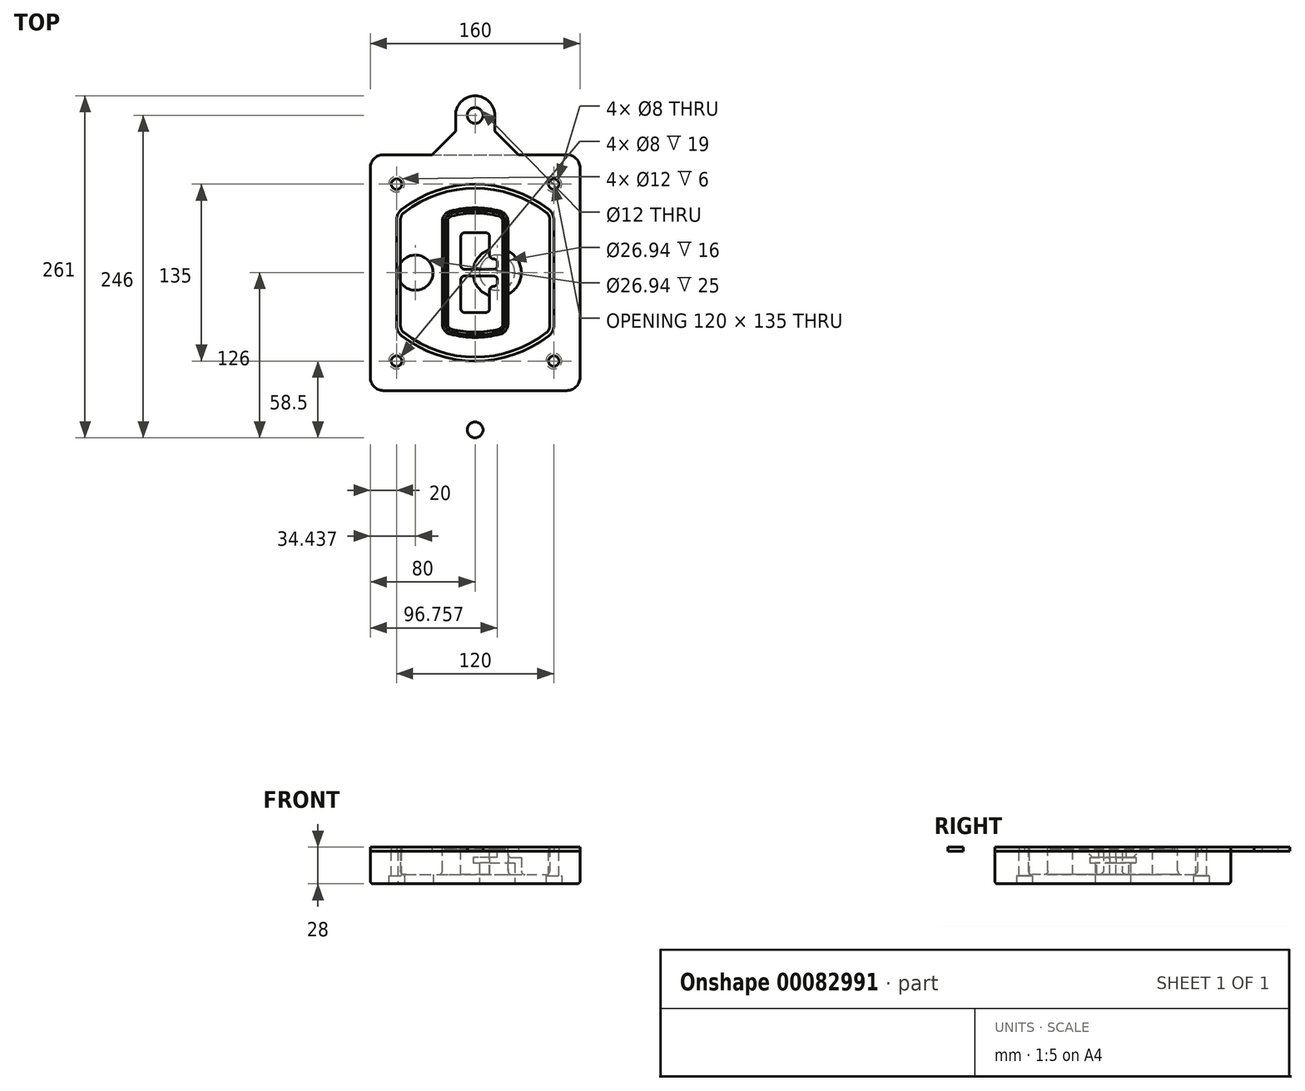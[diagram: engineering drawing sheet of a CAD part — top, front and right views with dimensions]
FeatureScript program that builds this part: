
annotation { "Feature Type Name" : "Feature", "Feature Type Description" : "" }
export const myFeature = defineFeature(function(context is Context, id is Id, definition is map)
    precondition{}
    {
        {
            var Q0;
            Q0=qCreatedBy(makeId("Top.planeOp"),FACE);
            var sketch = newSketch(context, id + "F0", { "sketchPlane" : qUnion([Q0])});
            skPoint(sketch, "E0.rect.middle", {"position": v(0, 0) * mm});
            skLineSegment(sketch, "E1.bottom", {"start": v(-70, -90) * mm, "end": v(70, -90) * mm});
            skLineSegment(sketch, "E1.top", {"start": v(-70, 90) * mm, "end": v(70, 90) * mm});
            skLineSegment(sketch, "E1.left", {"start": v(-80, -80) * mm, "end": v(-80, 80) * mm});
            skLineSegment(sketch, "E1.right", {"start": v(80, -80) * mm, "end": v(80, 80) * mm});
            skLineSegment(sketch, "E2", {"start": v(-80, 90) * mm, "end": v(80, -90) * mm, "construction": true});
            skLineSegment(sketch, "E3", {"start": v(80, 90) * mm, "end": v(-80, -90) * mm, "construction": true});
            skCircle(sketch, "E4", {"center": v(-60, 67.5) * mm, "radius": 4 * mm});
            skCircle(sketch, "E5", {"center": v(60, 67.5) * mm, "radius": 4 * mm});
            skCircle(sketch, "E6", {"center": v(60, -67.5) * mm, "radius": 4 * mm});
            skCircle(sketch, "E7", {"center": v(-60, -67.5) * mm, "radius": 4 * mm});
            skLineSegment(sketch, "E8", {"start": v(-60, 67.5) * mm, "end": v(60, 67.5) * mm, "construction": true});
            skLineSegment(sketch, "E9", {"start": v(60, 67.5) * mm, "end": v(60, -67.5) * mm, "construction": true});
            skLineSegment(sketch, "E10", {"start": v(60, -67.5) * mm, "end": v(-60, -67.5) * mm, "construction": true});
            skLineSegment(sketch, "E11", {"start": v(-60, -67.5) * mm, "end": v(-60, 67.5) * mm, "construction": true});
            skLineSegment(sketch, "E12", {"start": v(-60, 40.3) * mm, "end": v(-60, -40.3) * mm});
            skLineSegment(sketch, "E13", {"start": v(60, 40.3) * mm, "end": v(60, -40.3) * mm});
            skArc(sketch, "E14", {"start": v(56.15, 48.18) * mm, "mid": v(0, 67.5) * mm, "end": v(-56.15, 48.18) * mm});
            skArc(sketch, "E15", {"start": v(-56.15, -48.18) * mm, "mid": v(0, -67.5) * mm, "end": v(56.15, -48.18) * mm});
            skLineSegment(sketch, "E16", {"start": v(-60, 0) * mm, "end": v(60, 0) * mm, "construction": true});
            skPoint(sketch, "E17.visualSharp", {"position": v(-60, -45) * mm});
            skArc(sketch, "E17.filletArc", {"start": v(-60, -40.3) * mm, "mid": v(-58.99, -44.68) * mm, "end": v(-56.15, -48.18) * mm});
            skPoint(sketch, "E18.visualSharp", {"position": v(-60, 45) * mm});
            skArc(sketch, "E18.filletArc", {"start": v(-56.15, 48.18) * mm, "mid": v(-58.99, 44.68) * mm, "end": v(-60, 40.3) * mm});
            skPoint(sketch, "E19.visualSharp", {"position": v(60, 45) * mm});
            skArc(sketch, "E19.filletArc", {"start": v(60, 40.3) * mm, "mid": v(58.99, 44.68) * mm, "end": v(56.15, 48.18) * mm});
            skPoint(sketch, "E20.visualSharp", {"position": v(60, -45) * mm});
            skArc(sketch, "E20.filletArc", {"start": v(56.15, -48.18) * mm, "mid": v(58.99, -44.68) * mm, "end": v(60, -40.3) * mm});
            skPoint(sketch, "E21.visualSharp", {"position": v(-80, 90) * mm});
            skArc(sketch, "E21.filletArc", {"start": v(-70, 90) * mm, "mid": v(-77.07, 87.07) * mm, "end": v(-80, 80) * mm});
            skPoint(sketch, "E22.visualSharp", {"position": v(80, 90) * mm});
            skArc(sketch, "E22.filletArc", {"start": v(80, 80) * mm, "mid": v(77.07, 87.07) * mm, "end": v(70, 90) * mm});
            skPoint(sketch, "E23.visualSharp", {"position": v(80, -90) * mm});
            skArc(sketch, "E23.filletArc", {"start": v(70, -90) * mm, "mid": v(77.07, -87.07) * mm, "end": v(80, -80) * mm});
            skPoint(sketch, "E24.visualSharp", {"position": v(-80, -90) * mm});
            skArc(sketch, "E24.filletArc", {"start": v(-80, -80) * mm, "mid": v(-77.07, -87.07) * mm, "end": v(-70, -90) * mm});
            skArc(sketch, "E25.0", {"start": v(57, 40.3) * mm, "mid": v(56.3, 43.36) * mm, "end": v(54.3, 45.81) * mm});
            skLineSegment(sketch, "E25.1", {"start": v(57, 40.3) * mm, "end": v(57, -40.3) * mm});
            skArc(sketch, "E25.2", {"start": v(54.3, -45.81) * mm, "mid": v(56.3, -43.36) * mm, "end": v(57, -40.3) * mm});
            skArc(sketch, "E25.3", {"start": v(-54.3, -45.81) * mm, "mid": v(0, -64.5) * mm, "end": v(54.3, -45.81) * mm});
            skArc(sketch, "E25.4", {"start": v(-57, -40.3) * mm, "mid": v(-56.3, -43.36) * mm, "end": v(-54.3, -45.81) * mm});
            skArc(sketch, "E25.5", {"start": v(54.3, 45.81) * mm, "mid": v(0, 64.5) * mm, "end": v(-54.3, 45.81) * mm});
            skLineSegment(sketch, "E25.6", {"start": v(-57, 40.3) * mm, "end": v(-57, -40.3) * mm});
            skArc(sketch, "E25.7", {"start": v(-54.3, 45.81) * mm, "mid": v(-56.3, 43.36) * mm, "end": v(-57, 40.3) * mm});
            skArc(sketch, "E26.0", {"start": v(-58.62, 51.33) * mm, "mid": v(-62.58, 46.43) * mm, "end": v(-64, 40.3) * mm});
            skArc(sketch, "E26.1", {"start": v(58.62, 51.33) * mm, "mid": v(0, 71.5) * mm, "end": v(-58.62, 51.33) * mm});
            skArc(sketch, "E26.2", {"start": v(64, 40.3) * mm, "mid": v(62.58, 46.43) * mm, "end": v(58.62, 51.33) * mm});
            skLineSegment(sketch, "E26.3", {"start": v(64, 40.3) * mm, "end": v(64, -40.3) * mm});
            skArc(sketch, "E26.4", {"start": v(58.62, -51.33) * mm, "mid": v(62.58, -46.43) * mm, "end": v(64, -40.3) * mm});
            skLineSegment(sketch, "E26.5", {"start": v(-64, 40.3) * mm, "end": v(-64, -40.3) * mm});
            skArc(sketch, "E26.6", {"start": v(-58.62, -51.33) * mm, "mid": v(0, -71.5) * mm, "end": v(58.62, -51.33) * mm});
            skArc(sketch, "E26.7", {"start": v(-64, -40.3) * mm, "mid": v(-62.58, -46.43) * mm, "end": v(-58.62, -51.33) * mm});
            skSolve(sketch);
        }
        {
            var Q0;
            Q0=makeQuery(id+"F0.imprint","IMPRINT",FACE,{"disambiguationData":[TD([[makeQuery(id+"F0.imprint","IMPRINT",EDGE,{"derivedFrom":sQuery(id+"F0.wireOp",EDGE,"E1.bottom")}),1.0]])]});
            var Q1;
            Q1=makeQuery(id+"F0.imprint","IMPRINT",FACE,{"disambiguationData":[TD([[makeQuery(id+"F0.imprint","IMPRINT",EDGE,{"derivedFrom":sQuery(id+"F0.wireOp",EDGE,"E12")}),1.0]])]});
            var Q2;
            Q2=makeQuery(id+"F0.imprint","IMPRINT",FACE,{"disambiguationData":[TD([[makeQuery(id+"F0.imprint","IMPRINT",EDGE,{"derivedFrom":sQuery(id+"F0.wireOp",EDGE,"E25.0")}),1.0]])]});
            var Q3;
            Q3=makeQuery(id+"F0.imprint","IMPRINT",FACE,{"disambiguationData":[TD([[makeQuery(id+"F0.imprint","IMPRINT",EDGE,{"derivedFrom":sQuery(id+"F0.wireOp",EDGE,"E12")}),-1.0]])]});
            extrude(context, id + "F1", {"entities" : qUnion([Q0, Q1, Q2, Q3]), "oppositeDirection" : true, "depth" : 25 * mm});
        }
        {
            var Q0;
            Q0=makeQuery(id+"F0.imprint","IMPRINT",FACE,{"disambiguationData":[TD([[makeQuery(id+"F0.imprint","IMPRINT",EDGE,{"derivedFrom":sQuery(id+"F0.wireOp",EDGE,"E12")}),1.0]])]});
            extrude(context, id + "F2", {"entities" : qUnion([Q0]), "operationType" : NewBodyOperationType.ADD, "depth" : 3 * mm});
        }
        {
            var Q0;
            Q0=makeQuery(id+"F0.imprint","IMPRINT",FACE,{"disambiguationData":[TD([[makeQuery(id+"F0.imprint","IMPRINT",EDGE,{"derivedFrom":sQuery(id+"F0.wireOp",EDGE,"E25.0")}),1.0]])]});
            extrude(context, id + "F3", {"entities" : qUnion([Q0]), "operationType" : NewBodyOperationType.REMOVE, "oppositeDirection" : true, "depth" : 18 * mm});
        }
        {
            var Q0;
            Q0=makeQuery(id+"F2.opExtrude","CAP_FACE",FACE,{"disambiguationData":[OSD([sQuery(id+"F0.wireOp",EDGE,"E12"),sQuery(id+"F0.wireOp",EDGE,"E13"),sQuery(id+"F0.wireOp",EDGE,"E14"),sQuery(id+"F0.wireOp",EDGE,"E15"),sQuery(id+"F0.wireOp",EDGE,"E17.filletArc"),sQuery(id+"F0.wireOp",EDGE,"E18.filletArc"),sQuery(id+"F0.wireOp",EDGE,"E19.filletArc"),sQuery(id+"F0.wireOp",EDGE,"E20.filletArc"),sQuery(id+"F0.wireOp",EDGE,"E25.0"),sQuery(id+"F0.wireOp",EDGE,"E25.1"),sQuery(id+"F0.wireOp",EDGE,"E25.2"),sQuery(id+"F0.wireOp",EDGE,"E25.3"),sQuery(id+"F0.wireOp",EDGE,"E25.4"),sQuery(id+"F0.wireOp",EDGE,"E25.5"),sQuery(id+"F0.wireOp",EDGE,"E25.6"),sQuery(id+"F0.wireOp",EDGE,"E25.7")])],"isStart":false});
            var sketch = newSketch(context, id + "F4", { "sketchPlane" : qUnion([Q0])});
            skArc(sketch, "E27.0", {"start": v(-19.08, -46.97) * mm, "mid": v(0, -49.5) * mm, "end": v(19.08, -46.97) * mm});
            skArc(sketch, "E28.0", {"start": v(19.08, 46.97) * mm, "mid": v(0, 49.5) * mm, "end": v(-19.08, 46.97) * mm});
            skLineSegment(sketch, "E29", {"start": v(-25, 39.25) * mm, "end": v(-25, -39.25) * mm});
            skLineSegment(sketch, "E30", {"start": v(25, 39.25) * mm, "end": v(25, -39.25) * mm});
            skLineSegment(sketch, "E31", {"start": v(-25, 45.1) * mm, "end": v(25, 45.1) * mm, "construction": true});
            skLineSegment(sketch, "E32", {"start": v(-25, -45.1) * mm, "end": v(25, -45.1) * mm, "construction": true});
            skPoint(sketch, "E33.visualSharp", {"position": v(-25, 45.1) * mm});
            skArc(sketch, "E33.filletArc", {"start": v(-19.08, 46.97) * mm, "mid": v(-23.35, 44.11) * mm, "end": v(-25, 39.25) * mm});
            skPoint(sketch, "E34.visualSharp", {"position": v(25, 45.1) * mm});
            skArc(sketch, "E34.filletArc", {"start": v(25, 39.25) * mm, "mid": v(23.35, 44.11) * mm, "end": v(19.08, 46.97) * mm});
            skPoint(sketch, "E35.visualSharp", {"position": v(25, -45.1) * mm});
            skArc(sketch, "E35.filletArc", {"start": v(19.08, -46.97) * mm, "mid": v(23.35, -44.11) * mm, "end": v(25, -39.25) * mm});
            skPoint(sketch, "E36.visualSharp", {"position": v(-25, -45.1) * mm});
            skArc(sketch, "E36.filletArc", {"start": v(-25, -39.25) * mm, "mid": v(-23.35, -44.11) * mm, "end": v(-19.08, -46.97) * mm});
            skArc(sketch, "E37.0", {"start": v(54.3, 45.81) * mm, "mid": v(0, 64.5) * mm, "end": v(-54.3, 45.81) * mm});
            skArc(sketch, "E37.1", {"start": v(-54.3, 45.81) * mm, "mid": v(-56.3, 43.36) * mm, "end": v(-57, 40.3) * mm});
            skLineSegment(sketch, "E37.2", {"start": v(-57, 40.3) * mm, "end": v(-57, -40.3) * mm});
            skArc(sketch, "E37.3", {"start": v(-57, -40.3) * mm, "mid": v(-56.3, -43.36) * mm, "end": v(-54.3, -45.81) * mm});
            skArc(sketch, "E37.4", {"start": v(-54.3, -45.81) * mm, "mid": v(0, -64.5) * mm, "end": v(54.3, -45.81) * mm});
            skArc(sketch, "E37.5", {"start": v(54.3, -45.81) * mm, "mid": v(56.3, -43.36) * mm, "end": v(57, -40.3) * mm});
            skLineSegment(sketch, "E37.6", {"start": v(57, 40.3) * mm, "end": v(57, -40.3) * mm});
            skArc(sketch, "E37.7", {"start": v(57, 40.3) * mm, "mid": v(56.3, 43.36) * mm, "end": v(54.3, 45.81) * mm});
            skLineSegment(sketch, "E38.0", {"start": v(23, 39.25) * mm, "end": v(23, -39.25) * mm});
            skArc(sketch, "E38.1", {"start": v(18.56, -45.04) * mm, "mid": v(21.76, -42.9) * mm, "end": v(23, -39.25) * mm});
            skArc(sketch, "E38.2", {"start": v(-18.56, -45.04) * mm, "mid": v(0, -47.5) * mm, "end": v(18.56, -45.04) * mm});
            skArc(sketch, "E38.3", {"start": v(-23, -39.25) * mm, "mid": v(-21.76, -42.9) * mm, "end": v(-18.56, -45.04) * mm});
            skLineSegment(sketch, "E38.4", {"start": v(-23, 39.25) * mm, "end": v(-23, -39.25) * mm});
            skArc(sketch, "E38.5", {"start": v(23, 39.25) * mm, "mid": v(21.76, 42.9) * mm, "end": v(18.56, 45.04) * mm});
            skArc(sketch, "E38.6", {"start": v(-18.56, 45.04) * mm, "mid": v(-21.76, 42.9) * mm, "end": v(-23, 39.25) * mm});
            skArc(sketch, "E38.7", {"start": v(18.56, 45.04) * mm, "mid": v(0, 47.5) * mm, "end": v(-18.56, 45.04) * mm});
            skArc(sketch, "E39.0", {"start": v(21, 39.25) * mm, "mid": v(20.18, 41.68) * mm, "end": v(18.04, 43.1) * mm});
            skLineSegment(sketch, "E39.1", {"start": v(21, 39.25) * mm, "end": v(21, -39.25) * mm});
            skArc(sketch, "E39.2", {"start": v(18.04, -43.1) * mm, "mid": v(20.18, -41.68) * mm, "end": v(21, -39.25) * mm});
            skArc(sketch, "E39.3", {"start": v(-18.04, -43.1) * mm, "mid": v(0, -45.5) * mm, "end": v(18.04, -43.1) * mm});
            skArc(sketch, "E39.4", {"start": v(-21, -39.25) * mm, "mid": v(-20.18, -41.68) * mm, "end": v(-18.04, -43.1) * mm});
            skArc(sketch, "E39.5", {"start": v(18.04, 43.1) * mm, "mid": v(0, 45.5) * mm, "end": v(-18.04, 43.1) * mm});
            skLineSegment(sketch, "E39.6", {"start": v(-21, 39.25) * mm, "end": v(-21, -39.25) * mm});
            skArc(sketch, "E39.7", {"start": v(-18.04, 43.1) * mm, "mid": v(-20.18, 41.68) * mm, "end": v(-21, 39.25) * mm});
            skLineSegment(sketch, "E40", {"start": v(-25, 0) * mm, "end": v(25, 0) * mm, "construction": true});
            skLineSegment(sketch, "E41", {"start": v(-11, 5.5) * mm, "end": v(-11, 27.5) * mm});
            skLineSegment(sketch, "E42", {"start": v(-8, 30.5) * mm, "end": v(8, 30.5) * mm});
            skLineSegment(sketch, "E43", {"start": v(11, 27.5) * mm, "end": v(11, 13.5) * mm});
            skLineSegment(sketch, "E44", {"start": v(14, 10.5) * mm, "end": v(14, 10.5) * mm});
            skLineSegment(sketch, "E45", {"start": v(17, 7.5) * mm, "end": v(17, 5.5) * mm});
            skLineSegment(sketch, "E46", {"start": v(14, 2.5) * mm, "end": v(-8, 2.5) * mm});
            skPoint(sketch, "E47.visualSharp", {"position": v(-11, 30.5) * mm});
            skArc(sketch, "E47.filletArc", {"start": v(-8, 30.5) * mm, "mid": v(-10.12, 29.62) * mm, "end": v(-11, 27.5) * mm});
            skPoint(sketch, "E48.visualSharp", {"position": v(11, 30.5) * mm});
            skArc(sketch, "E48.filletArc", {"start": v(11, 27.5) * mm, "mid": v(10.12, 29.62) * mm, "end": v(8, 30.5) * mm});
            skPoint(sketch, "E49.visualSharp", {"position": v(11, 10.5) * mm});
            skArc(sketch, "E49.filletArc", {"start": v(11, 13.5) * mm, "mid": v(11.88, 11.38) * mm, "end": v(14, 10.5) * mm});
            skPoint(sketch, "E50.visualSharp", {"position": v(17, 10.5) * mm});
            skArc(sketch, "E50.filletArc", {"start": v(17, 7.5) * mm, "mid": v(16.12, 9.62) * mm, "end": v(14, 10.5) * mm});
            skPoint(sketch, "E51.visualSharp", {"position": v(17, 2.5) * mm});
            skArc(sketch, "E51.filletArc", {"start": v(14, 2.5) * mm, "mid": v(16.12, 3.38) * mm, "end": v(17, 5.5) * mm});
            skPoint(sketch, "E52.visualSharp", {"position": v(-11, 2.5) * mm});
            skArc(sketch, "E52.filletArc", {"start": v(-11, 5.5) * mm, "mid": v(-10.12, 3.38) * mm, "end": v(-8, 2.5) * mm});
            skLineSegment(sketch, "E53.0.MirrorCS", {"start": v(14, -2.5) * mm, "end": v(-8, -2.5) * mm});
            skArc(sketch, "E54.0.MirrorCS", {"start": v(-11, -5.5) * mm, "mid": v(-10.12, -3.38) * mm, "end": v(-8, -2.5) * mm});
            skLineSegment(sketch, "E55.0.MirrorCS", {"start": v(-11, -5.5) * mm, "end": v(-11, -27.5) * mm});
            skArc(sketch, "E56.0.MirrorCS", {"start": v(-8, -30.5) * mm, "mid": v(-10.12, -29.62) * mm, "end": v(-11, -27.5) * mm});
            skLineSegment(sketch, "E57.0.MirrorCS", {"start": v(-8, -30.5) * mm, "end": v(8, -30.5) * mm});
            skArc(sketch, "E58.0.MirrorCS", {"start": v(11, -27.5) * mm, "mid": v(10.12, -29.62) * mm, "end": v(8, -30.5) * mm});
            skLineSegment(sketch, "E59.0.MirrorCS", {"start": v(11, -27.5) * mm, "end": v(11, -13.5) * mm});
            skArc(sketch, "E60.0.MirrorCS", {"start": v(11, -13.5) * mm, "mid": v(11.88, -11.38) * mm, "end": v(14, -10.5) * mm});
            skArc(sketch, "E61.0.MirrorCS", {"start": v(17, -7.5) * mm, "mid": v(16.12, -9.62) * mm, "end": v(14, -10.5) * mm});
            skLineSegment(sketch, "E62.0.MirrorCS", {"start": v(17, -7.5) * mm, "end": v(17, -5.5) * mm});
            skArc(sketch, "E63.0.MirrorCS", {"start": v(14, -2.5) * mm, "mid": v(16.12, -3.38) * mm, "end": v(17, -5.5) * mm});
            skSolve(sketch);
        }
        {
            var Q0;
            Q0=makeQuery(id+"F4.imprint","IMPRINT",FACE,{"disambiguationData":[TD([[makeQuery(id+"F4.imprint","IMPRINT",EDGE,{"derivedFrom":sQuery(id+"F4.wireOp",EDGE,"E27.0")}),1.0]])]});
            var Q1;
            Q1=makeQuery(id+"F4.imprint","IMPRINT",FACE,{"disambiguationData":[TD([[makeQuery(id+"F4.imprint","IMPRINT",EDGE,{"derivedFrom":sQuery(id+"F4.wireOp",EDGE,"E38.0")}),-1.0]])]});
            var Q2;
            Q2=makeQuery(id+"F4.imprint","IMPRINT",FACE,{"disambiguationData":[TD([[makeQuery(id+"F4.imprint","IMPRINT",EDGE,{"derivedFrom":sQuery(id+"F4.wireOp",EDGE,"E39.0")}),1.0]])]});
            extrude(context, id + "F5", {"entities" : qUnion([Q0, Q1, Q2]), "operationType" : NewBodyOperationType.ADD, "endBound" : BoundingType.UP_TO_NEXT, "oppositeDirection" : true, "depth" : 25 * mm});
        }
        {
            var Q0;
            Q0=makeQuery(id+"F4.imprint","IMPRINT",FACE,{"disambiguationData":[TD([[makeQuery(id+"F4.imprint","IMPRINT",EDGE,{"derivedFrom":sQuery(id+"F4.wireOp",EDGE,"E38.0")}),-1.0]])]});
            extrude(context, id + "F6", {"entities" : qUnion([Q0]), "operationType" : NewBodyOperationType.REMOVE, "oppositeDirection" : true, "depth" : 2 * mm});
        }
        {
            var Q0;
            Q0=makeQuery(id+"F1.opExtrude","CAP_FACE",FACE,{"disambiguationData":[OSD([sQuery(id+"F0.wireOp",EDGE,"E1.bottom"),sQuery(id+"F0.wireOp",EDGE,"E1.top"),sQuery(id+"F0.wireOp",EDGE,"E1.left"),sQuery(id+"F0.wireOp",EDGE,"E1.right"),sQuery(id+"F0.wireOp",EDGE,"E4"),sQuery(id+"F0.wireOp",EDGE,"E5"),sQuery(id+"F0.wireOp",EDGE,"E6"),sQuery(id+"F0.wireOp",EDGE,"E7"),sQuery(id+"F0.wireOp",EDGE,"E21.filletArc"),sQuery(id+"F0.wireOp",EDGE,"E22.filletArc"),sQuery(id+"F0.wireOp",EDGE,"E23.filletArc"),sQuery(id+"F0.wireOp",EDGE,"E24.filletArc")])],"isStart":false});
            var sketch = newSketch(context, id + "F7", { "sketchPlane" : qUnion([Q0])});
            skCircle(sketch, "E64", {"center": v(16.76, 0) * mm, "radius": 13.47 * mm});
            skCircle(sketch, "E65", {"center": v(-45.56, 0) * mm, "radius": 13.47 * mm});
            skLineSegment(sketch, "E66", {"start": v(80, 0) * mm, "end": v(-80, 0) * mm});
            skCircle(sketch, "E67", {"center": v(16.76, 0) * mm, "radius": 18.47 * mm});
            skCircle(sketch, "E68", {"center": v(60, -67.5) * mm, "radius": 6 * mm});
            skCircle(sketch, "E69", {"center": v(-60, -67.5) * mm, "radius": 6 * mm});
            skCircle(sketch, "E70", {"center": v(-60, 67.5) * mm, "radius": 6 * mm});
            skCircle(sketch, "E71", {"center": v(60, 67.5) * mm, "radius": 6 * mm});
            skSolve(sketch);
        }
        {
            var Q0;
            {var subQ1=sQuery(id+"F7.wireOp",EDGE,"E66");var subQ4=sQuery(id+"F7.wireOp",EDGE,"E64");var subQ6=makeQuery(id+"F7.imprint","INTERSECT",VERTEX,{"disambiguationData":[OD(0.0)],"derivedFrom":[subQ4,subQ1]});Q0=makeQuery(id+"F7.imprint","IMPRINT",FACE,{"disambiguationData":[TD([[makeQuery(id+"F7.imprint","IMPRINT",EDGE,{"disambiguationData":[TD([[subQ6,-1.0]])],"derivedFrom":subQ4}),-1.0]])]});}
            var Q1;
            {var subQ0=sQuery(id+"F7.wireOp",EDGE,"E66");var subQ1=sQuery(id+"F7.wireOp",EDGE,"E64");var subQ3=makeQuery(id+"F7.imprint","INTERSECT",VERTEX,{"disambiguationData":[OD(0.0)],"derivedFrom":[subQ1,subQ0]});Q1=makeQuery(id+"F7.imprint","IMPRINT",FACE,{"disambiguationData":[TD([[makeQuery(id+"F7.imprint","IMPRINT",EDGE,{"disambiguationData":[TD([[subQ3,-1.0]])],"derivedFrom":subQ1}),1.0]])]});}
            var Q2;
            {var subQ0=sQuery(id+"F7.wireOp",EDGE,"E66");var subQ1=sQuery(id+"F7.wireOp",EDGE,"E64");var subQ3=makeQuery(id+"F7.imprint","INTERSECT",VERTEX,{"disambiguationData":[OD(0.0)],"derivedFrom":[subQ1,subQ0]});Q2=makeQuery(id+"F7.imprint","IMPRINT",FACE,{"disambiguationData":[TD([[makeQuery(id+"F7.imprint","IMPRINT",EDGE,{"disambiguationData":[TD([[subQ3,1.0]])],"derivedFrom":subQ1}),1.0]])]});}
            var Q3;
            {var subQ1=sQuery(id+"F7.wireOp",EDGE,"E66");var subQ4=sQuery(id+"F7.wireOp",EDGE,"E64");var subQ6=makeQuery(id+"F7.imprint","INTERSECT",VERTEX,{"disambiguationData":[OD(0.0)],"derivedFrom":[subQ4,subQ1]});Q3=makeQuery(id+"F7.imprint","IMPRINT",FACE,{"disambiguationData":[TD([[makeQuery(id+"F7.imprint","IMPRINT",EDGE,{"disambiguationData":[TD([[subQ6,1.0]])],"derivedFrom":subQ4}),-1.0]])]});}
            extrude(context, id + "F8", {"entities" : qUnion([Q0, Q1, Q2, Q3]), "operationType" : NewBodyOperationType.ADD, "oppositeDirection" : true, "depth" : 20 * mm});
        }
        {
            var Q0;
            {var subQ0=sQuery(id+"F7.wireOp",EDGE,"E66");var subQ1=sQuery(id+"F7.wireOp",EDGE,"E64");var subQ3=makeQuery(id+"F7.imprint","INTERSECT",VERTEX,{"disambiguationData":[OD(0.0)],"derivedFrom":[subQ1,subQ0]});Q0=makeQuery(id+"F7.imprint","IMPRINT",FACE,{"disambiguationData":[TD([[makeQuery(id+"F7.imprint","IMPRINT",EDGE,{"disambiguationData":[TD([[subQ3,-1.0]])],"derivedFrom":subQ1}),1.0]])]});}
            var Q1;
            {var subQ0=sQuery(id+"F7.wireOp",EDGE,"E66");var subQ1=sQuery(id+"F7.wireOp",EDGE,"E64");var subQ3=makeQuery(id+"F7.imprint","INTERSECT",VERTEX,{"disambiguationData":[OD(0.0)],"derivedFrom":[subQ1,subQ0]});Q1=makeQuery(id+"F7.imprint","IMPRINT",FACE,{"disambiguationData":[TD([[makeQuery(id+"F7.imprint","IMPRINT",EDGE,{"disambiguationData":[TD([[subQ3,1.0]])],"derivedFrom":subQ1}),1.0]])]});}
            extrude(context, id + "F9", {"entities" : qUnion([Q0, Q1]), "operationType" : NewBodyOperationType.REMOVE, "oppositeDirection" : true, "depth" : 16 * mm});
        }
        {
            var Q0;
            {var subQ0=sQuery(id+"F7.wireOp",EDGE,"E66");var subQ1=sQuery(id+"F7.wireOp",EDGE,"E65");var subQ3=makeQuery(id+"F7.imprint","INTERSECT",VERTEX,{"disambiguationData":[OD(0.0)],"derivedFrom":[subQ1,subQ0]});Q0=makeQuery(id+"F7.imprint","IMPRINT",FACE,{"disambiguationData":[TD([[makeQuery(id+"F7.imprint","IMPRINT",EDGE,{"disambiguationData":[TD([[subQ3,-1.0]])],"derivedFrom":subQ1}),1.0]])]});}
            var Q1;
            {var subQ0=sQuery(id+"F7.wireOp",EDGE,"E66");var subQ1=sQuery(id+"F7.wireOp",EDGE,"E65");var subQ3=makeQuery(id+"F7.imprint","INTERSECT",VERTEX,{"disambiguationData":[OD(0.0)],"derivedFrom":[subQ1,subQ0]});Q1=makeQuery(id+"F7.imprint","IMPRINT",FACE,{"disambiguationData":[TD([[makeQuery(id+"F7.imprint","IMPRINT",EDGE,{"disambiguationData":[TD([[subQ3,1.0]])],"derivedFrom":subQ1}),1.0]])]});}
            extrude(context, id + "F10", {"entities" : qUnion([Q0, Q1]), "operationType" : NewBodyOperationType.REMOVE, "oppositeDirection" : true, "depth" : 25 * mm});
        }
        {
            var Q0;
            Q0=makeQuery(id+"F7.imprint","IMPRINT",FACE,{"disambiguationData":[TD([[makeQuery(id+"F7.imprint","IMPRINT",EDGE,{"derivedFrom":sQuery(id+"F7.wireOp",EDGE,"E68")}),1.0]])]});
            var Q1;
            Q1=makeQuery(id+"F7.imprint","IMPRINT",FACE,{"disambiguationData":[TD([[makeQuery(id+"F7.imprint","IMPRINT",EDGE,{"derivedFrom":makeQuery(id+"F1.opExtrude","CAP_EDGE",EDGE,{"disambiguationData":[OSD([sQuery(id+"F0.wireOp",EDGE,"E5")])],"isStart":false})}),-1.0]])]});
            var Q2;
            Q2=makeQuery(id+"F7.imprint","IMPRINT",FACE,{"disambiguationData":[TD([[makeQuery(id+"F7.imprint","IMPRINT",EDGE,{"derivedFrom":sQuery(id+"F7.wireOp",EDGE,"E69")}),1.0]])]});
            var Q3;
            Q3=makeQuery(id+"F7.imprint","IMPRINT",FACE,{"disambiguationData":[TD([[makeQuery(id+"F7.imprint","IMPRINT",EDGE,{"derivedFrom":makeQuery(id+"F1.opExtrude","CAP_EDGE",EDGE,{"disambiguationData":[OSD([sQuery(id+"F0.wireOp",EDGE,"E4")])],"isStart":false})}),-1.0]])]});
            var Q4;
            Q4=makeQuery(id+"F7.imprint","IMPRINT",FACE,{"disambiguationData":[TD([[makeQuery(id+"F7.imprint","IMPRINT",EDGE,{"derivedFrom":sQuery(id+"F7.wireOp",EDGE,"E70")}),1.0]])]});
            var Q5;
            Q5=makeQuery(id+"F7.imprint","IMPRINT",FACE,{"disambiguationData":[TD([[makeQuery(id+"F7.imprint","IMPRINT",EDGE,{"derivedFrom":makeQuery(id+"F1.opExtrude","CAP_EDGE",EDGE,{"disambiguationData":[OSD([sQuery(id+"F0.wireOp",EDGE,"E7")])],"isStart":false})}),-1.0]])]});
            var Q6;
            Q6=makeQuery(id+"F7.imprint","IMPRINT",FACE,{"disambiguationData":[TD([[makeQuery(id+"F7.imprint","IMPRINT",EDGE,{"derivedFrom":sQuery(id+"F7.wireOp",EDGE,"E71")}),1.0]])]});
            var Q7;
            Q7=makeQuery(id+"F7.imprint","IMPRINT",FACE,{"disambiguationData":[TD([[makeQuery(id+"F7.imprint","IMPRINT",EDGE,{"derivedFrom":makeQuery(id+"F1.opExtrude","CAP_EDGE",EDGE,{"disambiguationData":[OSD([sQuery(id+"F0.wireOp",EDGE,"E6")])],"isStart":false})}),-1.0]])]});
            extrude(context, id + "F11", {"entities" : qUnion([Q0, Q1, Q2, Q3, Q4, Q5, Q6, Q7]), "operationType" : NewBodyOperationType.REMOVE, "oppositeDirection" : true, "depth" : 6 * mm});
        }
        {
            var Q0;
            Q0=makeQuery(id+"F9.boolean.opBoolean","COPY",FACE,{"derivedFrom":makeQuery(id+"F9.opExtrude","CAP_FACE",FACE,{"disambiguationData":[OSD([sQuery(id+"F7.wireOp",EDGE,"E64")])],"isStart":false})});
            var sketch = newSketch(context, id + "F12", { "sketchPlane" : qUnion([Q0])});
            skArc(sketch, "E72.0", {"start": v(11, 17.55) * mm, "mid": v(2.57, 11.82) * mm, "end": v(-1.54, 2.5) * mm});
            skArc(sketch, "E72.1", {"start": v(-1.54, -2.5) * mm, "mid": v(2.57, -11.82) * mm, "end": v(11, -17.55) * mm});
            skLineSegment(sketch, "E73", {"start": v(-1.54, -2.5) * mm, "end": v(14, -2.5) * mm});
            skLineSegment(sketch, "E74.0", {"start": v(14, 2.5) * mm, "end": v(-1.54, 2.5) * mm});
            skArc(sketch, "E74.1", {"start": v(14, 2.5) * mm, "mid": v(16.12, 3.38) * mm, "end": v(17, 5.5) * mm});
            skLineSegment(sketch, "E74.2", {"start": v(17, 7.5) * mm, "end": v(17, 5.5) * mm});
            skArc(sketch, "E74.3", {"start": v(17, 7.5) * mm, "mid": v(16.12, 9.62) * mm, "end": v(14, 10.5) * mm});
            skArc(sketch, "E74.4", {"start": v(11, 13.5) * mm, "mid": v(11.88, 11.38) * mm, "end": v(14, 10.5) * mm});
            skLineSegment(sketch, "E74.5", {"start": v(11, 17.55) * mm, "end": v(11, 13.5) * mm});
            skLineSegment(sketch, "E74.7", {"start": v(14, -2.5) * mm, "end": v(-1.54, -2.5) * mm});
            skArc(sketch, "E74.8", {"start": v(14, -2.5) * mm, "mid": v(16.12, -3.38) * mm, "end": v(17, -5.5) * mm});
            skLineSegment(sketch, "E74.9", {"start": v(17, -7.5) * mm, "end": v(17, -5.5) * mm});
            skArc(sketch, "E74.10", {"start": v(17, -7.5) * mm, "mid": v(16.12, -9.62) * mm, "end": v(14, -10.5) * mm});
            skArc(sketch, "E74.11", {"start": v(11, -13.5) * mm, "mid": v(11.88, -11.38) * mm, "end": v(14, -10.5) * mm});
            skLineSegment(sketch, "E74.12", {"start": v(11, -17.55) * mm, "end": v(11, -13.5) * mm});
            skPoint(sketch, "E75.orphan", {"position": v(11, -27.5) * mm});
            skPoint(sketch, "E76.orphan", {"position": v(-8, -2.5) * mm});
            skPoint(sketch, "E77.orphan", {"position": v(-8, 2.5) * mm});
            skPoint(sketch, "E78.orphan", {"position": v(11, 27.5) * mm});
            skSolve(sketch);
        }
        {
            var Q0;
            {var subQ7=sQuery(id+"F12.wireOp",EDGE,"E72.0");var subQ14=sQuery(id+"F12.wireOp",EDGE,"E72.1");var subQ16=sQuery(id+"F12.wireOp",EDGE,"E74.1");var subQ18=sQuery(id+"F12.wireOp",EDGE,"E74.8");Q0=qUnion([makeQuery(id+"F12.imprint","IMPRINT",FACE,{"disambiguationData":[TD([[makeQuery(id+"F12.imprint","IMPRINT",EDGE,{"derivedFrom":subQ7}),1.0]])]}),makeQuery(id+"F12.imprint","IMPRINT",FACE,{"disambiguationData":[TD([[makeQuery(id+"F12.imprint","IMPRINT",EDGE,{"derivedFrom":subQ14}),1.0]])]}),makeQuery(id+"F12.imprint","IMPRINT",FACE,{"disambiguationData":[TD([[makeQuery(id+"F12.imprint","IMPRINT",EDGE,{"derivedFrom":subQ16}),1.0]])]}),makeQuery(id+"F12.imprint","IMPRINT",FACE,{"disambiguationData":[TD([[makeQuery(id+"F12.imprint","IMPRINT",EDGE,{"derivedFrom":subQ18}),-1.0]])]})]);}
            var Q1;
            Q1=makeQuery(id+"F5.boolean.opBoolean","SPLIT",FACE,{"disambiguationData":[TD([makeQuery(id+"F5.opExtrude","SWEPT_FACE",FACE,{"disambiguationData":[OSD([sQuery(id+"F4.wireOp",EDGE,"E41")])]})])],"derivedFrom":makeQuery(id+"F3.boolean.opBoolean","COPY",FACE,{"derivedFrom":makeQuery(id+"F3.opExtrude","CAP_FACE",FACE,{"disambiguationData":[OSD([sQuery(id+"F0.wireOp",EDGE,"E25.0"),sQuery(id+"F0.wireOp",EDGE,"E25.1"),sQuery(id+"F0.wireOp",EDGE,"E25.2"),sQuery(id+"F0.wireOp",EDGE,"E25.3"),sQuery(id+"F0.wireOp",EDGE,"E25.4"),sQuery(id+"F0.wireOp",EDGE,"E25.5"),sQuery(id+"F0.wireOp",EDGE,"E25.6"),sQuery(id+"F0.wireOp",EDGE,"E25.7")])],"isStart":false})})});
            extrude(context, id + "F13", {"entities" : qUnion([Q0]), "operationType" : NewBodyOperationType.REMOVE, "endBound" : BoundingType.UP_TO_SURFACE, "endBoundEntityFace" : qUnion([Q1]), "depth" : 25 * mm});
        }
        {
            var Q0;
            Q0=makeQuery(id+"F3.boolean.opBoolean","COPY",EDGE,{"derivedFrom":makeQuery(id+"F3.opExtrude","CAP_EDGE",EDGE,{"disambiguationData":[OSD([sQuery(id+"F0.wireOp",EDGE,"E25.6")])],"isStart":false})});
            var Q1;
            Q1=makeQuery(id+"F8.boolean.opBoolean","INTERSECT",EDGE,{"derivedFrom":[makeQuery(id+"F5.opExtrude","SWEPT_FACE",FACE,{"disambiguationData":[OSD([sQuery(id+"F4.wireOp",EDGE,"E30")])]}),makeQuery(id+"F8.opExtrude","CAP_FACE",FACE,{"disambiguationData":[OSD([sQuery(id+"F7.wireOp",EDGE,"E67")])],"isStart":false})]});
            var Q2;
            Q2=makeQuery(id+"F8.boolean.opBoolean","INTERSECT",EDGE,{"disambiguationData":[OD(1.0)],"derivedFrom":[makeQuery(id+"F5.opExtrude","SWEPT_FACE",FACE,{"disambiguationData":[OSD([sQuery(id+"F4.wireOp",EDGE,"E30")])]}),makeQuery(id+"F8.opExtrude","SWEPT_FACE",FACE,{"disambiguationData":[OSD([sQuery(id+"F7.wireOp",EDGE,"E67")])]})]});
            var Q3;
            {var subQ0=sQuery(id+"F4.wireOp",EDGE,"E30");Q3=makeQuery(id+"F8.boolean.opBoolean","SPLIT",EDGE,{"disambiguationData":[TD([makeQuery(id+"F5.opExtrude","SWEPT_FACE",FACE,{"disambiguationData":[OSD([sQuery(id+"F4.wireOp",EDGE,"E35.filletArc")])]})])],"derivedFrom":makeQuery(id+"F5.opExtrude","CAP_EDGE",EDGE,{"disambiguationData":[OSD([subQ0])],"isStart":false})});}
            var Q4;
            {var subQ0=sQuery(id+"F0.wireOp",EDGE,"E25.7");var subQ1=sQuery(id+"F0.wireOp",EDGE,"E25.1");var subQ2=sQuery(id+"F0.wireOp",EDGE,"E25.6");var subQ3=sQuery(id+"F0.wireOp",EDGE,"E25.5");var subQ4=sQuery(id+"F0.wireOp",EDGE,"E25.4");var subQ5=sQuery(id+"F0.wireOp",EDGE,"E25.0");var subQ6=sQuery(id+"F0.wireOp",EDGE,"E25.2");var subQ7=sQuery(id+"F0.wireOp",EDGE,"E25.3");Q4=makeQuery(id+"F8.boolean.opBoolean","INTERSECT",EDGE,{"derivedFrom":[makeQuery(id+"F5.boolean.opBoolean","SPLIT",FACE,{"disambiguationData":[TD([makeQuery(id+"F2.opExtrude","SWEPT_FACE",FACE,{"disambiguationData":[OSD([subQ5])]})])],"derivedFrom":makeQuery(id+"F3.boolean.opBoolean","COPY",FACE,{"derivedFrom":makeQuery(id+"F3.opExtrude","CAP_FACE",FACE,{"disambiguationData":[OSD([subQ5,subQ1,subQ6,subQ7,subQ4,subQ3,subQ2,subQ0])],"isStart":false})})}),makeQuery(id+"F8.opExtrude","SWEPT_FACE",FACE,{"disambiguationData":[OSD([sQuery(id+"F7.wireOp",EDGE,"E67")])]})]});}
            var Q5;
            Q5=makeQuery(id+"F8.boolean.opBoolean","INTERSECT",EDGE,{"disambiguationData":[OD(0.0)],"derivedFrom":[makeQuery(id+"F5.opExtrude","SWEPT_FACE",FACE,{"disambiguationData":[OSD([sQuery(id+"F4.wireOp",EDGE,"E30")])]}),makeQuery(id+"F8.opExtrude","SWEPT_FACE",FACE,{"disambiguationData":[OSD([sQuery(id+"F7.wireOp",EDGE,"E67")])]})]});
            fillet(context, id + "F14", {"entities" : qUnion([Q0, Q1, Q2, Q3, Q4, Q5]), "radius" : 3 * mm, "tangentPropagation" : true, "allowEdgeOverflow" : false});
        }
        {
            var Q0;
            Q0=makeQuery(id+"F1.opExtrude","CAP_EDGE",EDGE,{"disambiguationData":[OSD([sQuery(id+"F0.wireOp",EDGE,"E1.bottom")])],"isStart":false});
            fillet(context, id + "F15", {"entities" : qUnion([Q0]), "radius" : 2 * mm, "tangentPropagation" : true, "allowEdgeOverflow" : false});
        }
        {
            var Q0;
            {var subQ0=sQuery(id+"F0.wireOp",EDGE,"E22.filletArc");var subQ1=sQuery(id+"F0.wireOp",EDGE,"E7");var subQ2=sQuery(id+"F0.wireOp",EDGE,"E6");var subQ3=sQuery(id+"F0.wireOp",EDGE,"E5");var subQ4=sQuery(id+"F0.wireOp",EDGE,"E4");var subQ5=sQuery(id+"F0.wireOp",EDGE,"E1.bottom");var subQ6=sQuery(id+"F0.wireOp",EDGE,"E21.filletArc");var subQ7=sQuery(id+"F0.wireOp",EDGE,"E1.top");var subQ8=sQuery(id+"F0.wireOp",EDGE,"E1.left");var subQ9=sQuery(id+"F0.wireOp",EDGE,"E1.right");var subQ10=sQuery(id+"F0.wireOp",EDGE,"E23.filletArc");var subQ11=sQuery(id+"F0.wireOp",EDGE,"E24.filletArc");Q0=makeQuery(id+"F2.boolean.opBoolean","SPLIT",FACE,{"disambiguationData":[TD([makeQuery(id+"F1.opExtrude","SWEPT_FACE",FACE,{"disambiguationData":[OSD([subQ5])]})])],"derivedFrom":makeQuery(id+"F1.opExtrude","CAP_FACE",FACE,{"disambiguationData":[OSD([subQ5,subQ7,subQ8,subQ9,subQ4,subQ3,subQ2,subQ1,subQ6,subQ0,subQ10,subQ11])],"isStart":true})});}
            var sketch = newSketch(context, id + "F16", { "sketchPlane" : qUnion([Q0])});
            skLineSegment(sketch, "E79", {"start": v(-33, 90) * mm, "end": v(-15, 108) * mm});
            skLineSegment(sketch, "E80", {"start": v(-15, 108) * mm, "end": v(-15, 120) * mm});
            skLineSegment(sketch, "E81", {"start": v(0, 90) * mm, "end": v(0, 120) * mm, "construction": true});
            skCircle(sketch, "E82", {"center": v(0, 120) * mm, "radius": 6 * mm});
            skLineSegment(sketch, "E83", {"start": v(15, 120) * mm, "end": v(15, 108) * mm});
            skLineSegment(sketch, "E84", {"start": v(15, 108) * mm, "end": v(33, 90) * mm});
            skArc(sketch, "E85", {"start": v(15, 120) * mm, "mid": v(0, 135) * mm, "end": v(-15, 120) * mm});
            skLineSegment(sketch, "E86", {"start": v(-80, 0) * mm, "end": v(80, 0) * mm, "construction": true});
            skLineSegment(sketch, "E87.MirrorCS", {"start": v(33, 90) * mm, "end": v(15, 108) * mm});
            skLineSegment(sketch, "E88.MirrorCS", {"start": v(15, 108) * mm, "end": v(15, 120) * mm});
            skLineSegment(sketch, "E89.MirrorCS", {"start": v(-15, 120) * mm, "end": v(-15, 108) * mm});
            skArc(sketch, "E90.MirrorCS", {"start": v(-15, 120) * mm, "mid": v(0, 135) * mm, "end": v(15, 120) * mm});
            skLineSegment(sketch, "E91.MirrorCS", {"start": v(-15, 108) * mm, "end": v(-33, 90) * mm});
            skLineSegment(sketch, "E92.MirrorCS", {"start": v(80, 0) * mm, "end": v(-80, 0) * mm, "construction": true});
            skCircle(sketch, "E93.MirrorC", {"center": v(0, -120) * mm, "radius": 6 * mm});
            skLineSegment(sketch, "E94.MirrorCS", {"start": v(15, -120) * mm, "end": v(15, -108) * mm});
            skLineSegment(sketch, "E95.MirrorCS", {"start": v(-15, -108) * mm, "end": v(-33, -90) * mm});
            skLineSegment(sketch, "E96.MirrorCS", {"start": v(33, -90) * mm, "end": v(15, -108) * mm});
            skArc(sketch, "E97.MirrorCS", {"start": v(-15, -120) * mm, "mid": v(0, -135) * mm, "end": v(15, -120) * mm});
            skLineSegment(sketch, "E98.MirrorCS", {"start": v(-15, -120) * mm, "end": v(-15, -108) * mm});
            skLineSegment(sketch, "E99.MirrorCS", {"start": v(15, -108) * mm, "end": v(33, -90) * mm});
            skArc(sketch, "E100.MirrorCS", {"start": v(15, -120) * mm, "mid": v(0, -135) * mm, "end": v(-15, -120) * mm});
            skLineSegment(sketch, "E101.MirrorCS", {"start": v(-15, -108) * mm, "end": v(-15, -120) * mm});
            skLineSegment(sketch, "E102.MirrorCS", {"start": v(15, -108) * mm, "end": v(15, -120) * mm});
            skLineSegment(sketch, "E103.MirrorCS", {"start": v(-33, -90) * mm, "end": v(-15, -108) * mm});
            skLineSegment(sketch, "E104.MirrorCS", {"start": v(0, -90) * mm, "end": v(0, -120) * mm, "construction": true});
            skSolve(sketch);
        }
        {
            var Q0;
            Q0=makeQuery(id+"F16.imprint","IMPRINT",FACE,{"disambiguationData":[TD([[makeQuery(id+"F16.imprint","IMPRINT",EDGE,{"derivedFrom":sQuery(id+"F16.wireOp",EDGE,"E85")}),1.0]])]});
            var Q1;
            Q1=makeQuery(id+"F16.imprint","IMPRINT",FACE,{"disambiguationData":[TD([[makeQuery(id+"F16.imprint","IMPRINT",EDGE,{"derivedFrom":makeQuery(id+"F1.opExtrude","CAP_EDGE",EDGE,{"disambiguationData":[OSD([sQuery(id+"F0.wireOp",EDGE,"E1.left")])],"isStart":true})}),-1.0]])]});
            var Q2;
            Q2=makeQuery(id+"F16.imprint","IMPRINT",FACE,{"disambiguationData":[TD([[makeQuery(id+"F16.imprint","IMPRINT",EDGE,{"derivedFrom":sQuery(id+"F16.wireOp",EDGE,"E93.MirrorC")}),1.0]])]});
            var Q3;
            Q3=makeQuery(id+"F2.opExtrude","CAP_FACE",FACE,{"disambiguationData":[OSD([sQuery(id+"F0.wireOp",EDGE,"E12"),sQuery(id+"F0.wireOp",EDGE,"E13"),sQuery(id+"F0.wireOp",EDGE,"E14"),sQuery(id+"F0.wireOp",EDGE,"E15"),sQuery(id+"F0.wireOp",EDGE,"E17.filletArc"),sQuery(id+"F0.wireOp",EDGE,"E18.filletArc"),sQuery(id+"F0.wireOp",EDGE,"E19.filletArc"),sQuery(id+"F0.wireOp",EDGE,"E20.filletArc"),sQuery(id+"F0.wireOp",EDGE,"E25.0"),sQuery(id+"F0.wireOp",EDGE,"E25.1"),sQuery(id+"F0.wireOp",EDGE,"E25.2"),sQuery(id+"F0.wireOp",EDGE,"E25.3"),sQuery(id+"F0.wireOp",EDGE,"E25.4"),sQuery(id+"F0.wireOp",EDGE,"E25.5"),sQuery(id+"F0.wireOp",EDGE,"E25.6"),sQuery(id+"F0.wireOp",EDGE,"E25.7")])],"isStart":false});
            extrude(context, id + "F17", {"entities" : qUnion([Q0, Q1, Q2]), "endBound" : BoundingType.UP_TO_SURFACE, "endBoundEntityFace" : qUnion([Q3]), "depth" : 25 * mm});
        }
    });
